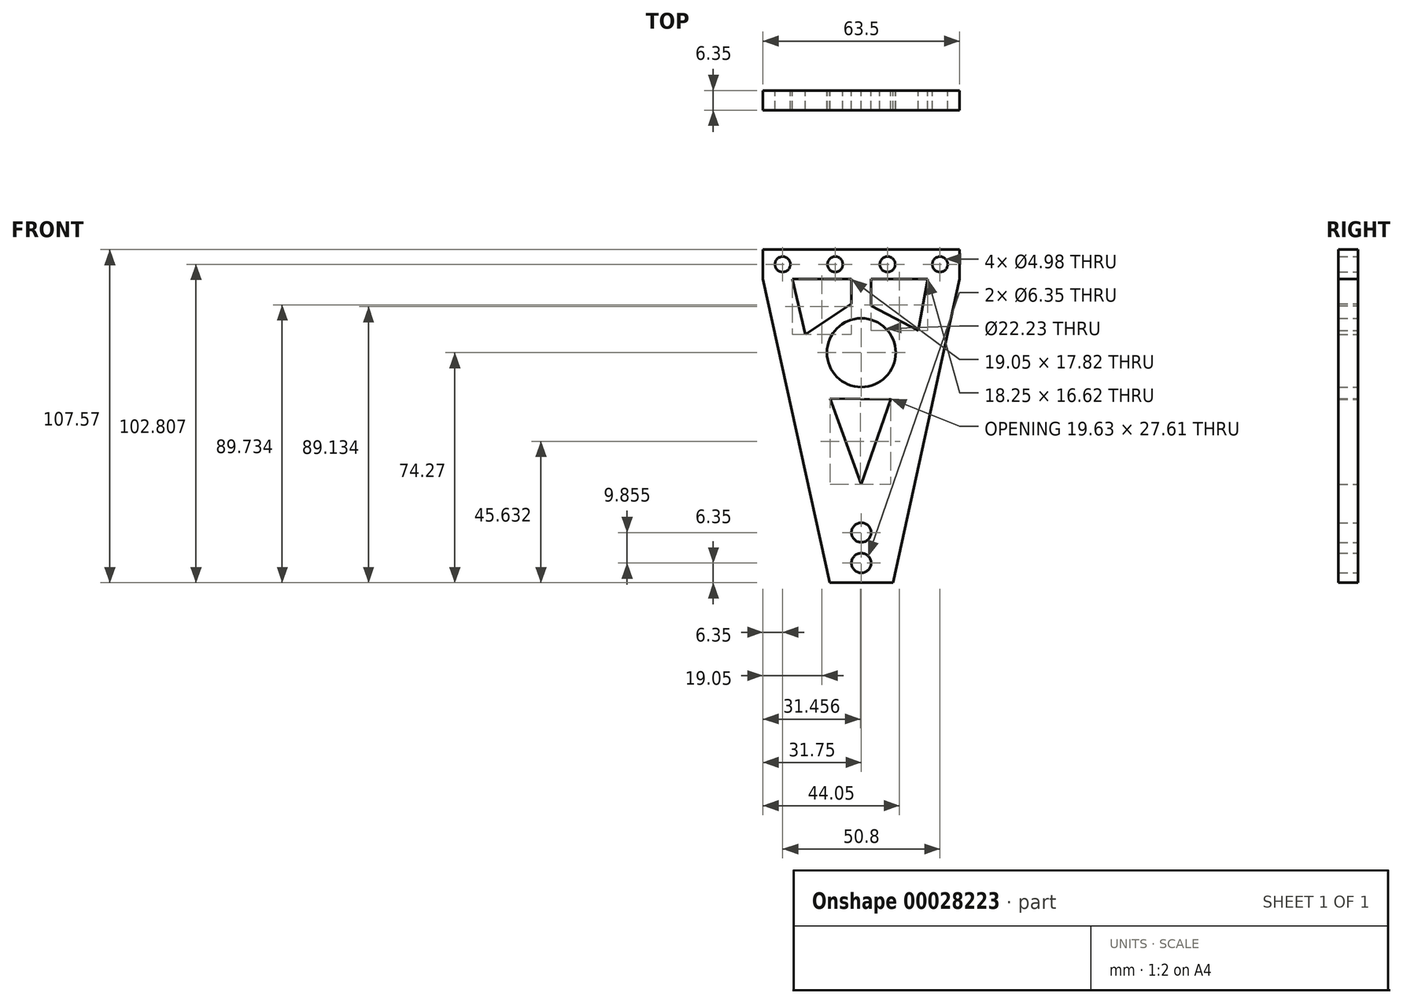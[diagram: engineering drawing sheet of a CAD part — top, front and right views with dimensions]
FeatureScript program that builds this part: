
annotation { "Feature Type Name" : "Feature", "Feature Type Description" : "" }
export const myFeature = defineFeature(function(context is Context, id is Id, definition is map)
    precondition{}
    {
        {
            var Q0;
            Q0=qCreatedBy(makeId("Front.planeOp"),FACE);
            var sketch = newSketch(context, id + "F0", { "sketchPlane" : qUnion([Q0])});
            skLineSegment(sketch, "E0", {"start": v(-31.75, 33.3) * mm, "end": v(-31.75, 23.77) * mm});
            skLineSegment(sketch, "E1", {"start": v(-31.75, 23.77) * mm, "end": v(-10.25, -74.27) * mm});
            skLineSegment(sketch, "E2", {"start": v(-10.25, -74.27) * mm, "end": v(10.25, -74.27) * mm});
            skLineSegment(sketch, "E3", {"start": v(10.25, -74.27) * mm, "end": v(31.75, 23.77) * mm});
            skLineSegment(sketch, "E4", {"start": v(31.75, 23.77) * mm, "end": v(31.75, 33.3) * mm});
            skLineSegment(sketch, "E5", {"start": v(31.75, 33.3) * mm, "end": v(-31.75, 33.3) * mm});
            skLineSegment(sketch, "E6", {"start": v(0, 47.7) * mm, "end": v(0, -77.72) * mm, "construction": true});
            skLineSegment(sketch, "E7", {"start": v(31.75, 28.54) * mm, "end": v(-31.75, 28.54) * mm, "construction": true});
            skCircle(sketch, "E8", {"center": v(-25.4, 28.54) * mm, "radius": 2.49 * mm});
            skCircle(sketch, "E9", {"center": v(-8.46, 28.54) * mm, "radius": 2.49 * mm});
            skCircle(sketch, "E10", {"center": v(8.46, 28.54) * mm, "radius": 2.49 * mm});
            skCircle(sketch, "E11", {"center": v(25.4, 28.54) * mm, "radius": 2.49 * mm});
            skCircle(sketch, "E12", {"center": v(0, 0) * mm, "radius": 11.11 * mm});
            skCircle(sketch, "E13", {"center": v(0, -58.06) * mm, "radius": 3.18 * mm});
            skCircle(sketch, "E14", {"center": v(0, -67.92) * mm, "radius": 3.18 * mm});
            skLineSegment(sketch, "E15", {"start": v(-22.23, 23.77) * mm, "end": v(-3.17, 23.77) * mm});
            skLineSegment(sketch, "E16", {"start": v(3.18, 23.77) * mm, "end": v(21.42, 23.77) * mm});
            skLineSegment(sketch, "E17", {"start": v(-22.23, 23.77) * mm, "end": v(-18.1, 5.95) * mm});
            skLineSegment(sketch, "E18", {"start": v(-18.1, 5.95) * mm, "end": v(-3.17, 15.78) * mm});
            skLineSegment(sketch, "E19", {"start": v(-3.17, 15.78) * mm, "end": v(-3.17, 23.77) * mm});
            skLineSegment(sketch, "E20", {"start": v(3.18, 23.77) * mm, "end": v(3.18, 15.2) * mm});
            skLineSegment(sketch, "E21", {"start": v(3.18, 15.2) * mm, "end": v(18.35, 7.15) * mm});
            skLineSegment(sketch, "E22", {"start": v(18.35, 7.15) * mm, "end": v(21.42, 23.77) * mm});
            skLineSegment(sketch, "E23", {"start": v(-10.1, -14.83) * mm, "end": v(9.52, -15) * mm});
            skPoint(sketch, "E23.endSnap0", {"position": v(0, -15) * mm});
            skLineSegment(sketch, "E24", {"start": v(9.52, -15) * mm, "end": v(0, -42.44) * mm});
            skLineSegment(sketch, "E25", {"start": v(0, -42.44) * mm, "end": v(-10.1, -14.83) * mm});
            skSolve(sketch);
        }
        {
            var Q0;
            Q0=makeQuery(id+"F0.imprint","IMPRINT",FACE,{"disambiguationData":[TD([[makeQuery(id+"F0.imprint","IMPRINT",EDGE,{"derivedFrom":sQuery(id+"F0.wireOp",EDGE,"E0")}),1.0]])]});
            extrude(context, id + "F1", {"entities" : qUnion([Q0]), "depth" : 6.35 * mm});
        }
    });
